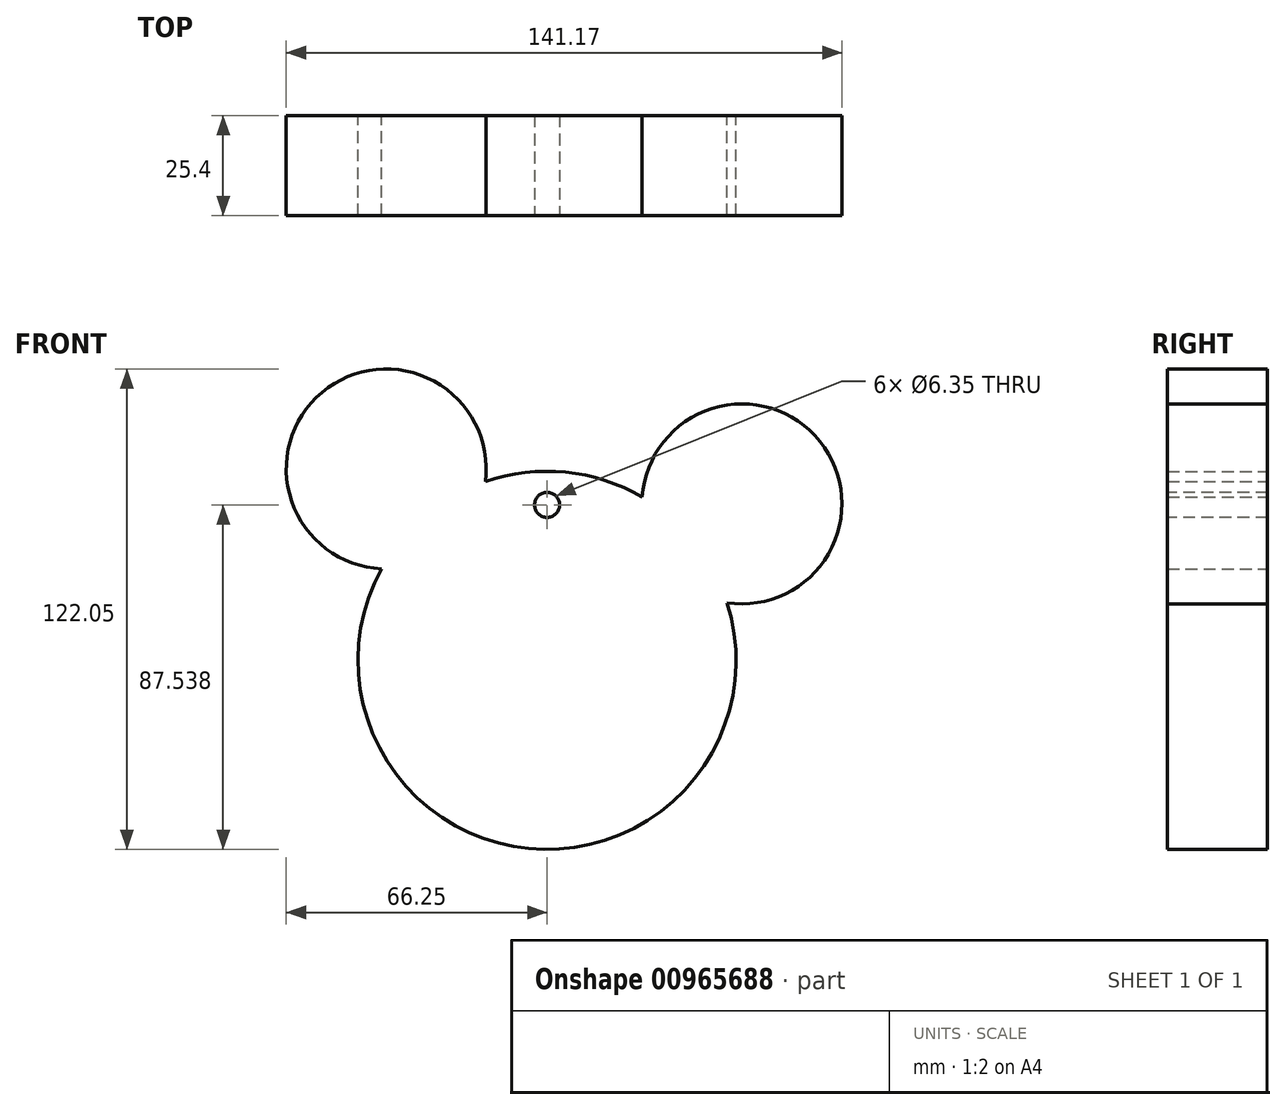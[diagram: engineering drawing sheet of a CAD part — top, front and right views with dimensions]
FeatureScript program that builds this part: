
annotation { "Feature Type Name" : "Feature", "Feature Type Description" : "" }
export const myFeature = defineFeature(function(context is Context, id is Id, definition is map)
    precondition{}
    {
        {
            var Q0;
            Q0=qCreatedBy(makeId("Front.planeOp"),FACE);
            var sketch = newSketch(context, id + "F0", { "sketchPlane" : qUnion([Q0])});
            skCircle(sketch, "E0", {"center": v(0, 0) * mm, "radius": 48.03 * mm});
            skCircle(sketch, "E1", {"center": v(-40.85, 48.62) * mm, "radius": 25.4 * mm});
            skCircle(sketch, "E2", {"center": v(49.52, 39.75) * mm, "radius": 25.4 * mm});
            skSolve(sketch);
        }
        {
            var Q0;
            {var subQ0=sQuery(id+"F0.wireOp",EDGE,"E2");var subQ1=sQuery(id+"F0.wireOp",EDGE,"E0");var subQ2=makeQuery(id+"F0.imprint","INTERSECT",VERTEX,{"disambiguationData":[OD(0.0)],"derivedFrom":[subQ1,subQ0]});Q0=makeQuery(id+"F0.imprint","IMPRINT",FACE,{"disambiguationData":[TD([[makeQuery(id+"F0.imprint","IMPRINT",EDGE,{"disambiguationData":[TD([[subQ2,-1.0]])],"derivedFrom":subQ1}),1.0]])]});}
            var Q1;
            {var subQ0=sQuery(id+"F0.wireOp",EDGE,"E2");var subQ1=sQuery(id+"F0.wireOp",EDGE,"E0");var subQ2=makeQuery(id+"F0.imprint","INTERSECT",VERTEX,{"disambiguationData":[OD(0.0)],"derivedFrom":[subQ1,subQ0]});Q1=makeQuery(id+"F0.imprint","IMPRINT",FACE,{"disambiguationData":[TD([[makeQuery(id+"F0.imprint","IMPRINT",EDGE,{"disambiguationData":[TD([[subQ2,1.0]])],"derivedFrom":subQ1}),-1.0]])]});}
            var Q2;
            {var subQ0=sQuery(id+"F0.wireOp",EDGE,"E2");var subQ1=sQuery(id+"F0.wireOp",EDGE,"E0");var subQ2=makeQuery(id+"F0.imprint","INTERSECT",VERTEX,{"disambiguationData":[OD(0.0)],"derivedFrom":[subQ1,subQ0]});Q2=makeQuery(id+"F0.imprint","IMPRINT",FACE,{"disambiguationData":[TD([[makeQuery(id+"F0.imprint","IMPRINT",EDGE,{"disambiguationData":[TD([[subQ2,1.0]])],"derivedFrom":subQ1}),1.0]])]});}
            var Q3;
            {var subQ0=sQuery(id+"F0.wireOp",EDGE,"E1");var subQ1=sQuery(id+"F0.wireOp",EDGE,"E0");var subQ2=makeQuery(id+"F0.imprint","INTERSECT",VERTEX,{"disambiguationData":[OD(0.0)],"derivedFrom":[subQ1,subQ0]});Q3=makeQuery(id+"F0.imprint","IMPRINT",FACE,{"disambiguationData":[TD([[makeQuery(id+"F0.imprint","IMPRINT",EDGE,{"disambiguationData":[TD([[subQ2,-1.0]])],"derivedFrom":subQ1}),1.0]])]});}
            var Q4;
            {var subQ0=sQuery(id+"F0.wireOp",EDGE,"E1");var subQ1=sQuery(id+"F0.wireOp",EDGE,"E0");var subQ2=makeQuery(id+"F0.imprint","INTERSECT",VERTEX,{"disambiguationData":[OD(0.0)],"derivedFrom":[subQ1,subQ0]});Q4=makeQuery(id+"F0.imprint","IMPRINT",FACE,{"disambiguationData":[TD([[makeQuery(id+"F0.imprint","IMPRINT",EDGE,{"disambiguationData":[TD([[subQ2,-1.0]])],"derivedFrom":subQ1}),-1.0]])]});}
            extrude(context, id + "F1", {"entities" : qUnion([Q0, Q1, Q2, Q3, Q4]), "depth" : 25.4 * mm, "offsetDistance" : 25.4 * mm});
        }
        {
            var Q0;
            Q0=makeQuery(id+"F1.opExtrude","CAP_FACE",FACE,{"disambiguationData":[OSD([sQuery(id+"F0.wireOp",EDGE,"E0"),sQuery(id+"F0.wireOp",EDGE,"E1"),sQuery(id+"F0.wireOp",EDGE,"E2")])],"isStart":false});
            var sketch = newSketch(context, id + "F2", { "sketchPlane" : qUnion([Q0])});
            skCircle(sketch, "E3", {"center": v(0, 39.5) * mm, "radius": 3.18 * mm});
            skSolve(sketch);
        }
        {
            var Q0;
            Q0=makeQuery(id+"F2.imprint","IMPRINT",FACE,{"disambiguationData":[TD([[makeQuery(id+"F2.imprint","IMPRINT",EDGE,{"derivedFrom":sQuery(id+"F2.wireOp",EDGE,"E3")}),1.0]])]});
            extrude(context, id + "F3", {"entities" : qUnion([Q0]), "operationType" : NewBodyOperationType.REMOVE, "endBound" : BoundingType.THROUGH_ALL, "oppositeDirection" : true, "depth" : 25.4 * mm, "offsetDistance" : 25.4 * mm});
        }
    });
